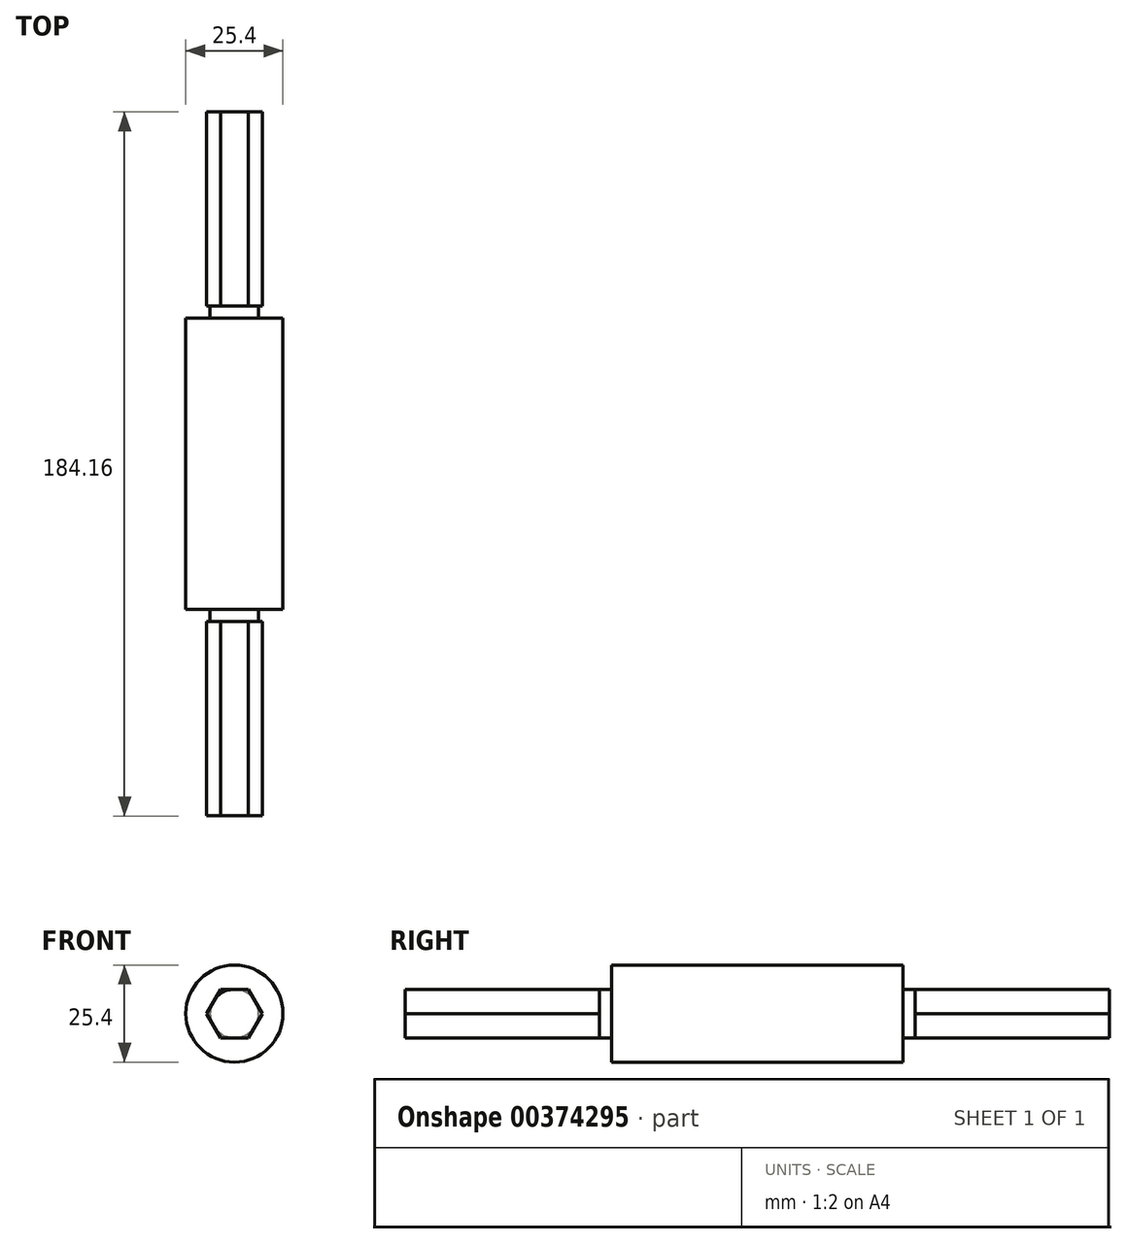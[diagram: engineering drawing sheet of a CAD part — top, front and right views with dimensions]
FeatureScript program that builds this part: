
annotation { "Feature Type Name" : "Feature", "Feature Type Description" : "" }
export const myFeature = defineFeature(function(context is Context, id is Id, definition is map)
    precondition{}
    {
        {
            var Q0;
            Q0=qCreatedBy(makeId("Top.planeOp"),FACE);
            var sketch = newSketch(context, id + "F0", { "sketchPlane" : qUnion([Q0])});
            skLineSegment(sketch, "E0", {"start": v(0, 41.27) * mm, "end": v(6.35, 41.27) * mm});
            skLineSegment(sketch, "E1", {"start": v(6.35, 41.27) * mm, "end": v(6.35, 38.1) * mm});
            skLineSegment(sketch, "E2", {"start": v(6.35, 38.1) * mm, "end": v(12.7, 38.1) * mm});
            skLineSegment(sketch, "E3", {"start": v(12.7, 38.1) * mm, "end": v(12.7, -38.1) * mm});
            skLineSegment(sketch, "E4", {"start": v(12.7, -38.1) * mm, "end": v(6.35, -38.1) * mm});
            skLineSegment(sketch, "E5", {"start": v(6.35, -38.1) * mm, "end": v(6.35, -41.27) * mm});
            skLineSegment(sketch, "E6", {"start": v(6.35, -41.27) * mm, "end": v(0, -41.27) * mm});
            skLineSegment(sketch, "E7", {"start": v(6.35, 38.1) * mm, "end": v(0, 38.1) * mm});
            skLineSegment(sketch, "E8", {"start": v(6.35, -38.1) * mm, "end": v(0, -38.1) * mm});
            skLineSegment(sketch, "E9", {"start": v(0, 0) * mm, "end": v(0, 38.1) * mm, "construction": true});
            skPoint(sketch, "E9.startSnap0", {"position": v(12.7, 0) * mm});
            skLineSegment(sketch, "E10", {"start": v(0, 41.27) * mm, "end": v(0, -41.27) * mm});
            skSolve(sketch);
        }
        {
            var Q0;
            Q0 = qSketchRegion(id + "F0", true);
            var Q1;
            Q1=sQuery(id+"F0.wireOp",EDGE,"E10");
            revolve(context, id + "F1", {"entities" : qUnion([Q0]), "axis" : qUnion([Q1]), "revolveType" : RevolveType.FULL});
        }
        {
            var Q0;
            Q0=makeQuery(id+"F1.opRevolve","SWEPT_FACE",FACE,{"disambiguationData":[OSD([sQuery(id+"F0.wireOp",EDGE,"E6")])]});
            var sketch = newSketch(context, id + "F2", { "sketchPlane" : qUnion([Q0])});
            skCircle(sketch, "E11.cCircle", {"center": v(0, 0) * mm, "radius": 6.35 * mm, "construction": true});
            skLineSegment(sketch, "E11.0", {"start": v(3.67, 6.35) * mm, "end": v(7.33, 0) * mm});
            skLineSegment(sketch, "E11.1", {"start": v(7.33, 0) * mm, "end": v(3.67, -6.35) * mm});
            skLineSegment(sketch, "E11.2", {"start": v(3.67, -6.35) * mm, "end": v(-3.67, -6.35) * mm});
            skLineSegment(sketch, "E11.3", {"start": v(-3.67, -6.35) * mm, "end": v(-7.33, 0) * mm});
            skLineSegment(sketch, "E11.4", {"start": v(-7.33, 0) * mm, "end": v(-3.67, 6.35) * mm});
            skLineSegment(sketch, "E11.5", {"start": v(-3.67, 6.35) * mm, "end": v(3.67, 6.35) * mm});
            skPoint(sketch, "E11.0.midPoint", {"position": v(5.5, 3.18) * mm});
            skSolve(sketch);
        }
        {
            var Q0;
            Q0 = qSketchRegion(id + "F2", true);
            extrude(context, id + "F3", {"entities" : qUnion([Q0]), "operationType" : NewBodyOperationType.ADD, "depth" : 50.8 * mm});
        }
        {
            var Q0;
            Q0=makeQuery(id+"F1.opRevolve","SWEPT_FACE",FACE,{"disambiguationData":[OSD([sQuery(id+"F0.wireOp",EDGE,"E0")])]});
            var sketch = newSketch(context, id + "F4", { "sketchPlane" : qUnion([Q0])});
            skCircle(sketch, "E12.cCircle", {"center": v(0, 0) * mm, "radius": 6.35 * mm, "construction": true});
            skLineSegment(sketch, "E12.0", {"start": v(3.67, 6.35) * mm, "end": v(7.33, 0) * mm});
            skLineSegment(sketch, "E12.1", {"start": v(7.33, 0) * mm, "end": v(3.67, -6.35) * mm});
            skLineSegment(sketch, "E12.2", {"start": v(3.67, -6.35) * mm, "end": v(-3.67, -6.35) * mm});
            skLineSegment(sketch, "E12.3", {"start": v(-3.67, -6.35) * mm, "end": v(-7.33, 0) * mm});
            skLineSegment(sketch, "E12.4", {"start": v(-7.33, 0) * mm, "end": v(-3.67, 6.35) * mm});
            skLineSegment(sketch, "E12.5", {"start": v(-3.67, 6.35) * mm, "end": v(3.67, 6.35) * mm});
            skPoint(sketch, "E12.0.midPoint", {"position": v(5.5, 3.18) * mm});
            skSolve(sketch);
        }
        {
            var Q0;
            Q0 = qSketchRegion(id + "F4", true);
            extrude(context, id + "F5", {"entities" : qUnion([Q0]), "operationType" : NewBodyOperationType.ADD, "depth" : 50.8 * mm});
        }
    });
